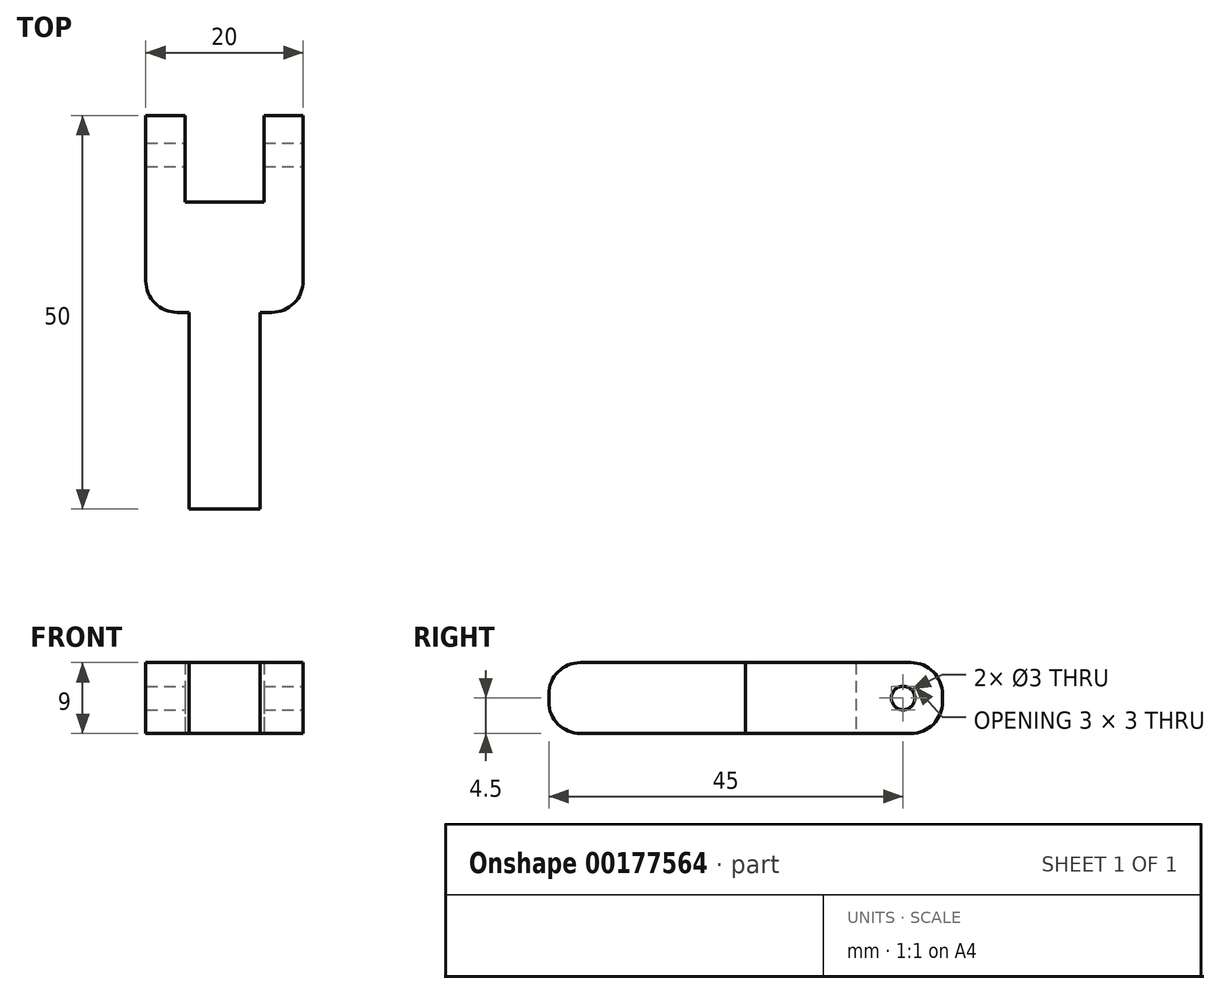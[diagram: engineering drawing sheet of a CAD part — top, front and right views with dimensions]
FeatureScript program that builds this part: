
annotation { "Feature Type Name" : "Feature", "Feature Type Description" : "" }
export const myFeature = defineFeature(function(context is Context, id is Id, definition is map)
    precondition{}
    {
        {
            var Q0;
            Q0=qCreatedBy(makeId("Top.planeOp"),FACE);
            var sketch = newSketch(context, id + "F0", { "sketchPlane" : qUnion([Q0])});
            skLineSegment(sketch, "E0.bottom", {"start": v(-10, 25) * mm, "end": v(-5, 25) * mm});
            skLineSegment(sketch, "E0.top", {"start": v(-4.5, -25) * mm, "end": v(4.5, -25) * mm});
            skLineSegment(sketch, "E0.left", {"start": v(-10, 25) * mm, "end": v(-10, 0) * mm});
            skLineSegment(sketch, "E0.right", {"start": v(10, 25) * mm, "end": v(10, 0) * mm});
            skPoint(sketch, "E0.middle", {"position": v(0, 0) * mm});
            skLineSegment(sketch, "E1.bottom", {"start": v(-10, 0) * mm, "end": v(-4.5, 0) * mm});
            skLineSegment(sketch, "E1.right", {"start": v(-4.5, 0) * mm, "end": v(-4.5, -25) * mm});
            skLineSegment(sketch, "E2.bottom", {"start": v(5, 14) * mm, "end": v(-5, 14) * mm});
            skLineSegment(sketch, "E2.left", {"start": v(5, 14) * mm, "end": v(5, 25) * mm});
            skLineSegment(sketch, "E2.right", {"start": v(-5, 14) * mm, "end": v(-5, 25) * mm});
            skPoint(sketch, "E2.middle", {"position": v(0, 25) * mm});
            skLineSegment(sketch, "E3.MirrorCS", {"start": v(10, 0) * mm, "end": v(4.5, 0) * mm});
            skLineSegment(sketch, "E4.MirrorCS", {"start": v(4.5, 0) * mm, "end": v(4.5, -25) * mm});
            skPoint(sketch, "E2.top.end.orphan", {"position": v(-5, 36) * mm});
            skPoint(sketch, "E5.orphan", {"position": v(5, 36) * mm});
            skLineSegment(sketch, "E6.trimOffspring", {"start": v(5, 25) * mm, "end": v(10, 25) * mm});
            skPoint(sketch, "E7.orphan", {"position": v(-10, -25) * mm});
            skPoint(sketch, "E8.orphan", {"position": v(10, -25) * mm});
            skSolve(sketch);
        }
        {
            var Q0;
            Q0=makeQuery(id+"F0.imprint","IMPRINT",FACE,{"disambiguationData":[TD([[makeQuery(id+"F0.imprint","IMPRINT",EDGE,{"derivedFrom":sQuery(id+"F0.wireOp",EDGE,"E0.bottom")}),-1.0]])]});
            extrude(context, id + "F1", {"entities" : qUnion([Q0]), "endBound" : BoundingType.SYMMETRIC, "depth" : 9 * mm});
        }
        {
            var Q0;
            Q0=makeQuery(id+"F1.opExtrude","SWEPT_FACE",FACE,{"disambiguationData":[OSD([sQuery(id+"F0.wireOp",EDGE,"E0.right")])]});
            var sketch = newSketch(context, id + "F2", { "sketchPlane" : qUnion([Q0])});
            skCircle(sketch, "E9", {"center": v(20, 0) * mm, "radius": 1.5 * mm});
            skCircle(sketch, "E10.MirrorC", {"center": v(-20, 0) * mm, "radius": 1.5 * mm});
            skSolve(sketch);
        }
        {
            var Q0;
            Q0=makeQuery(id+"F2.imprint","IMPRINT",FACE,{"disambiguationData":[TD([[makeQuery(id+"F2.imprint","IMPRINT",EDGE,{"derivedFrom":sQuery(id+"F2.wireOp",EDGE,"E9")}),1.0]])]});
            var Q1;
            Q1=makeQuery(id+"F2.imprint","IMPRINT",FACE,{"disambiguationData":[TD([[makeQuery(id+"F2.imprint","IMPRINT",EDGE,{"derivedFrom":sQuery(id+"F2.wireOp",EDGE,"E10.MirrorC")}),-1.0]])]});
            var Q2;
            Q2=sQuery(id+"F2.wireOp",EDGE,"E9");
            extrude(context, id + "F3", {"entities" : qUnion([Q0, Q1]), "operationType" : NewBodyOperationType.REMOVE, "surfaceEntities" : qUnion([Q2]), "endBound" : BoundingType.THROUGH_ALL, "oppositeDirection" : true, "depth" : 25 * mm});
        }
        {
            var Q0;
            Q0=makeQuery(id+"F1.opExtrude","CAP_EDGE",EDGE,{"disambiguationData":[OSD([sQuery(id+"F0.wireOp",EDGE,"E0.bottom")])],"isStart":false});
            var Q1;
            Q1=makeQuery(id+"F1.opExtrude","SWEPT_EDGE",EDGE,{"disambiguationData":[OSD([sQuery(id+"F0.wireOp",EDGE,"E0.right"),sQuery(id+"F0.wireOp",EDGE,"E3.MirrorCS")])]});
            var Q2;
            Q2=makeQuery(id+"F1.opExtrude","SWEPT_EDGE",EDGE,{"disambiguationData":[OSD([sQuery(id+"F0.wireOp",EDGE,"E0.left"),sQuery(id+"F0.wireOp",EDGE,"E1.bottom")])]});
            var Q3;
            Q3=makeQuery(id+"F1.opExtrude","CAP_EDGE",EDGE,{"disambiguationData":[OSD([sQuery(id+"F0.wireOp",EDGE,"E0.top")])],"isStart":false});
            var Q4;
            Q4=makeQuery(id+"F1.opExtrude","CAP_EDGE",EDGE,{"disambiguationData":[OSD([sQuery(id+"F0.wireOp",EDGE,"E0.top")])],"isStart":true});
            var Q5;
            Q5=makeQuery(id+"F1.opExtrude","CAP_EDGE",EDGE,{"disambiguationData":[OSD([sQuery(id+"F0.wireOp",EDGE,"E0.bottom")])],"isStart":true});
            var Q6;
            Q6=makeQuery(id+"F1.opExtrude","CAP_EDGE",EDGE,{"disambiguationData":[OSD([sQuery(id+"F0.wireOp",EDGE,"E6.trimOffspring")])],"isStart":true});
            var Q7;
            Q7=makeQuery(id+"F1.opExtrude","CAP_EDGE",EDGE,{"disambiguationData":[OSD([sQuery(id+"F0.wireOp",EDGE,"E6.trimOffspring")])],"isStart":false});
            fillet(context, id + "F4", {"entities" : qUnion([Q0, Q1, Q2, Q3, Q4, Q5, Q6, Q7]), "radius" : 4 * mm, "tangentPropagation" : true, "allowEdgeOverflow" : false});
        }
    });
